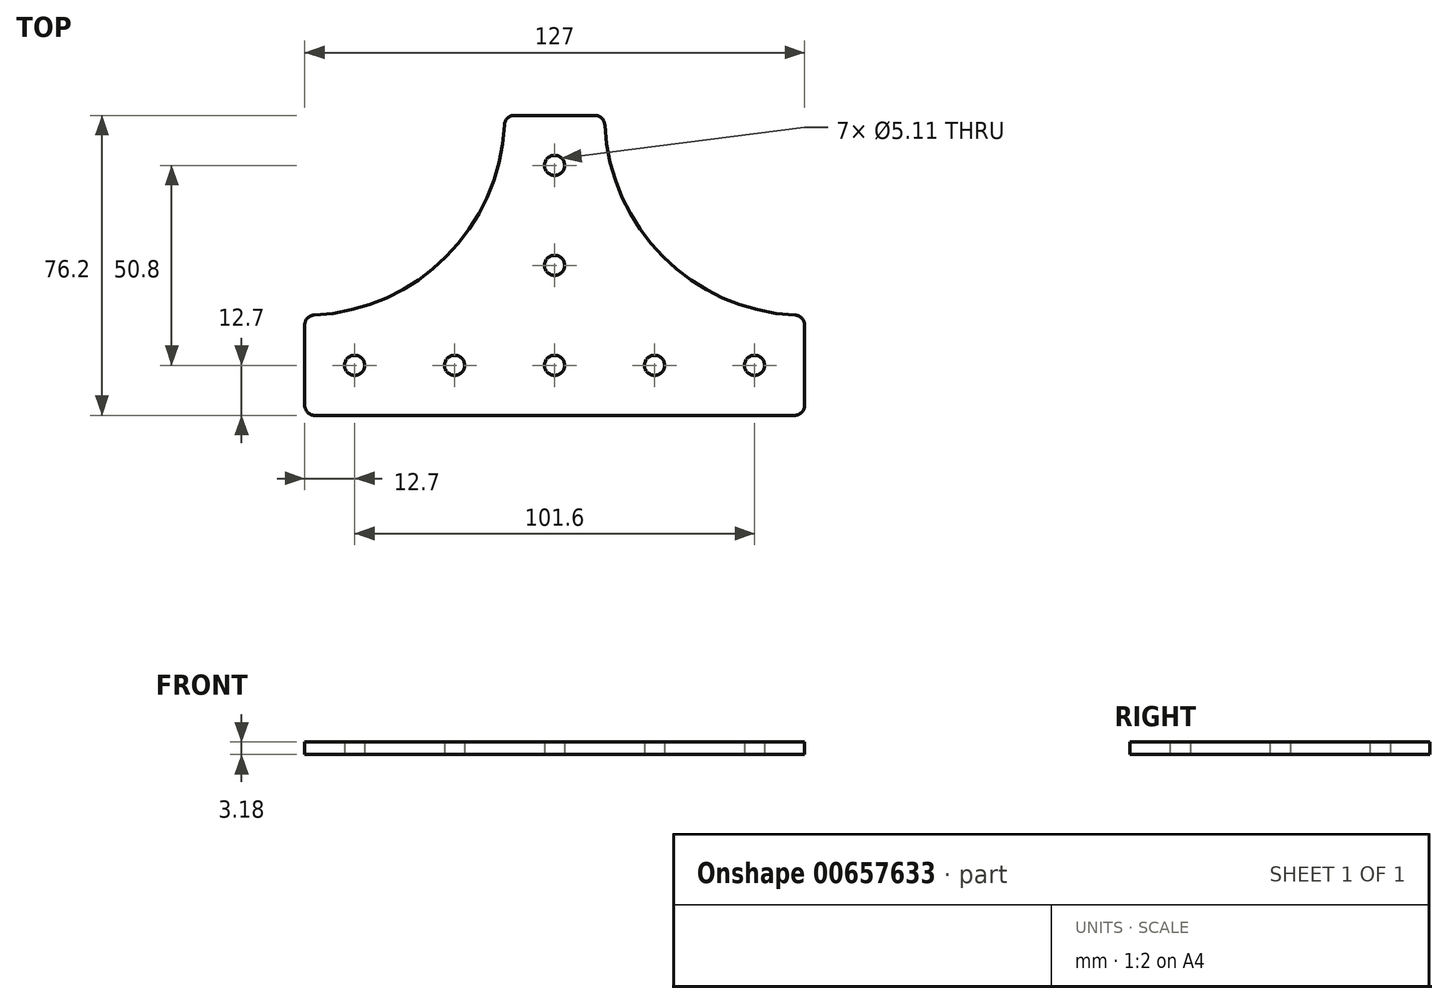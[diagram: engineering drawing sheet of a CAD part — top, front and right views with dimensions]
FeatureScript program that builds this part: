
annotation { "Feature Type Name" : "Feature", "Feature Type Description" : "" }
export const myFeature = defineFeature(function(context is Context, id is Id, definition is map)
    precondition{}
    {
        {
            var Q0;
            Q0=qCreatedBy(makeId("Top.planeOp"),FACE);
            var sketch = newSketch(context, id + "F0", { "sketchPlane" : qUnion([Q0])});
            skLineSegment(sketch, "E0", {"start": v(0, 0) * mm, "end": v(25.4, 0) * mm});
            skLineSegment(sketch, "E1", {"start": v(25.4, 0) * mm, "end": v(25.4, -50.8) * mm});
            skLineSegment(sketch, "E2", {"start": v(25.4, -50.8) * mm, "end": v(76.2, -50.8) * mm});
            skLineSegment(sketch, "E3", {"start": v(76.2, -50.8) * mm, "end": v(76.2, -76.2) * mm});
            skLineSegment(sketch, "E4", {"start": v(76.2, -76.2) * mm, "end": v(-50.8, -76.2) * mm});
            skLineSegment(sketch, "E5", {"start": v(-50.8, -76.2) * mm, "end": v(-50.8, -50.8) * mm});
            skLineSegment(sketch, "E6", {"start": v(-50.8, -50.8) * mm, "end": v(0, -50.8) * mm});
            skLineSegment(sketch, "E7", {"start": v(0, -50.8) * mm, "end": v(0, 0) * mm});
            skCircle(sketch, "E8", {"center": v(-38.1, -63.5) * mm, "radius": 2.55 * mm});
            skCircle(sketch, "E9.0.1.0", {"center": v(-38.1, -38.1) * mm, "radius": 2.55 * mm, "construction": true});
            skCircle(sketch, "E9.0.2.0", {"center": v(-38.1, -12.7) * mm, "radius": 2.55 * mm, "construction": true});
            skCircle(sketch, "E9.0.3.0", {"center": v(-38.1, 12.7) * mm, "radius": 2.55 * mm, "construction": true});
            skCircle(sketch, "E9.1.0.0", {"center": v(-12.7, -63.5) * mm, "radius": 2.55 * mm});
            skCircle(sketch, "E9.1.1.0", {"center": v(-12.7, -38.1) * mm, "radius": 2.55 * mm, "construction": true});
            skCircle(sketch, "E9.1.2.0", {"center": v(-12.7, -12.7) * mm, "radius": 2.55 * mm, "construction": true});
            skCircle(sketch, "E9.1.3.0", {"center": v(-12.7, 12.7) * mm, "radius": 2.55 * mm, "construction": true});
            skCircle(sketch, "E9.2.0.0", {"center": v(12.7, -63.5) * mm, "radius": 2.55 * mm});
            skCircle(sketch, "E9.2.1.0", {"center": v(12.7, -38.1) * mm, "radius": 2.55 * mm});
            skCircle(sketch, "E9.2.2.0", {"center": v(12.7, -12.7) * mm, "radius": 2.55 * mm});
            skCircle(sketch, "E9.2.3.0", {"center": v(12.7, 12.7) * mm, "radius": 2.55 * mm, "construction": true});
            skCircle(sketch, "E9.3.0.0", {"center": v(38.1, -63.5) * mm, "radius": 2.55 * mm});
            skCircle(sketch, "E9.3.1.0", {"center": v(38.1, -38.1) * mm, "radius": 2.55 * mm, "construction": true});
            skCircle(sketch, "E9.3.2.0", {"center": v(38.1, -12.7) * mm, "radius": 2.55 * mm, "construction": true});
            skCircle(sketch, "E9.3.3.0", {"center": v(38.1, 12.7) * mm, "radius": 2.55 * mm, "construction": true});
            skCircle(sketch, "E9.4.0.0", {"center": v(63.5, -63.5) * mm, "radius": 2.55 * mm});
            skCircle(sketch, "E9.4.1.0", {"center": v(63.5, -38.1) * mm, "radius": 2.55 * mm, "construction": true});
            skCircle(sketch, "E9.4.2.0", {"center": v(63.5, -12.7) * mm, "radius": 2.55 * mm, "construction": true});
            skCircle(sketch, "E9.4.3.0", {"center": v(63.5, 12.7) * mm, "radius": 2.55 * mm, "construction": true});
            skCircle(sketch, "E9.5.0.0", {"center": v(88.9, -63.5) * mm, "radius": 2.55 * mm, "construction": true});
            skCircle(sketch, "E9.5.1.0", {"center": v(88.9, -38.1) * mm, "radius": 2.55 * mm, "construction": true});
            skCircle(sketch, "E9.5.2.0", {"center": v(88.9, -12.7) * mm, "radius": 2.55 * mm, "construction": true});
            skCircle(sketch, "E9.5.3.0", {"center": v(88.9, 12.7) * mm, "radius": 2.55 * mm, "construction": true});
            skCircle(sketch, "E9.6.0.0", {"center": v(114.3, -63.5) * mm, "radius": 2.55 * mm, "construction": true});
            skCircle(sketch, "E9.6.1.0", {"center": v(114.3, -38.1) * mm, "radius": 2.55 * mm, "construction": true});
            skCircle(sketch, "E9.6.2.0", {"center": v(114.3, -12.7) * mm, "radius": 2.55 * mm, "construction": true});
            skCircle(sketch, "E9.6.3.0", {"center": v(114.3, 12.7) * mm, "radius": 2.55 * mm, "construction": true});
            skLineSegment(sketch, "E9.direction1", {"start": v(-38.1, -63.5) * mm, "end": v(-12.7, -63.5) * mm, "construction": true});
            skLineSegment(sketch, "E9.direction2", {"start": v(-38.1, -63.5) * mm, "end": v(-38.1, -38.1) * mm, "construction": true});
            skSolve(sketch);
        }
        {
            var Q0;
            Q0=makeQuery(id+"F0.imprint","IMPRINT",FACE,{"disambiguationData":[TD([[makeQuery(id+"F0.imprint","IMPRINT",EDGE,{"derivedFrom":sQuery(id+"F0.wireOp",EDGE,"E0")}),-1.0]])]});
            extrude(context, id + "F1", {"entities" : qUnion([Q0]), "depth" : 3.17 * mm, "offsetDistance" : 25.4 * mm});
        }
        {
            var Q0;
            Q0=makeQuery(id+"F1.opExtrude","SWEPT_EDGE",EDGE,{"disambiguationData":[OSD([sQuery(id+"F0.wireOp",EDGE,"E1"),sQuery(id+"F0.wireOp",EDGE,"E2")])]});
            var Q1;
            Q1=makeQuery(id+"F1.opExtrude","SWEPT_EDGE",EDGE,{"disambiguationData":[OSD([sQuery(id+"F0.wireOp",EDGE,"E6"),sQuery(id+"F0.wireOp",EDGE,"E7")])]});
            fillet(context, id + "F2", {"entities" : qUnion([Q0, Q1]), "tangentPropagation" : true, "radius" : 50.8 * mm, "defaultsChanged" : false, "vertexSettings" : [], "allowEdgeOverflow" : false});
        }
        {
            var Q0;
            Q0=makeQuery(id+"F2.opFillet","BLEND_EDGE",EDGE,{"blendedFrom":[makeQuery(id+"F1.opExtrude","SWEPT_EDGE",EDGE,{"disambiguationData":[OSD([sQuery(id+"F0.wireOp",EDGE,"E1"),sQuery(id+"F0.wireOp",EDGE,"E2")])]}),makeQuery(id+"F1.opExtrude","SWEPT_FACE",FACE,{"disambiguationData":[OSD([sQuery(id+"F0.wireOp",EDGE,"E0")])]})],"blendedInto":[makeQuery(id+"F1.opExtrude","SWEPT_FACE",FACE,{"disambiguationData":[OSD([sQuery(id+"F0.wireOp",EDGE,"E0")])]})]});
            var Q1;
            Q1=makeQuery(id+"F2.opFillet","BLEND_EDGE",EDGE,{"blendedFrom":[makeQuery(id+"F1.opExtrude","SWEPT_EDGE",EDGE,{"disambiguationData":[OSD([sQuery(id+"F0.wireOp",EDGE,"E1"),sQuery(id+"F0.wireOp",EDGE,"E2")])]}),makeQuery(id+"F1.opExtrude","SWEPT_FACE",FACE,{"disambiguationData":[OSD([sQuery(id+"F0.wireOp",EDGE,"E3")])]})],"blendedInto":[makeQuery(id+"F1.opExtrude","SWEPT_FACE",FACE,{"disambiguationData":[OSD([sQuery(id+"F0.wireOp",EDGE,"E3")])]})]});
            var Q2;
            Q2=makeQuery(id+"F1.opExtrude","SWEPT_EDGE",EDGE,{"disambiguationData":[OSD([sQuery(id+"F0.wireOp",EDGE,"E3"),sQuery(id+"F0.wireOp",EDGE,"E4")])]});
            var Q3;
            Q3=makeQuery(id+"F1.opExtrude","SWEPT_EDGE",EDGE,{"disambiguationData":[OSD([sQuery(id+"F0.wireOp",EDGE,"E4"),sQuery(id+"F0.wireOp",EDGE,"E5")])]});
            var Q4;
            Q4=makeQuery(id+"F2.opFillet","BLEND_EDGE",EDGE,{"blendedFrom":[makeQuery(id+"F1.opExtrude","SWEPT_EDGE",EDGE,{"disambiguationData":[OSD([sQuery(id+"F0.wireOp",EDGE,"E6"),sQuery(id+"F0.wireOp",EDGE,"E7")])]}),makeQuery(id+"F1.opExtrude","SWEPT_FACE",FACE,{"disambiguationData":[OSD([sQuery(id+"F0.wireOp",EDGE,"E5")])]})],"blendedInto":[makeQuery(id+"F1.opExtrude","SWEPT_FACE",FACE,{"disambiguationData":[OSD([sQuery(id+"F0.wireOp",EDGE,"E5")])]})]});
            var Q5;
            Q5=makeQuery(id+"F2.opFillet","BLEND_EDGE",EDGE,{"blendedFrom":[makeQuery(id+"F1.opExtrude","SWEPT_EDGE",EDGE,{"disambiguationData":[OSD([sQuery(id+"F0.wireOp",EDGE,"E6"),sQuery(id+"F0.wireOp",EDGE,"E7")])]}),makeQuery(id+"F1.opExtrude","SWEPT_FACE",FACE,{"disambiguationData":[OSD([sQuery(id+"F0.wireOp",EDGE,"E0")])]})],"blendedInto":[makeQuery(id+"F1.opExtrude","SWEPT_FACE",FACE,{"disambiguationData":[OSD([sQuery(id+"F0.wireOp",EDGE,"E0")])]})]});
            fillet(context, id + "F3", {"entities" : qUnion([Q0, Q1, Q2, Q3, Q4, Q5]), "tangentPropagation" : true, "radius" : 2.54 * mm, "defaultsChanged" : false, "vertexSettings" : [], "allowEdgeOverflow" : false});
        }
    });
